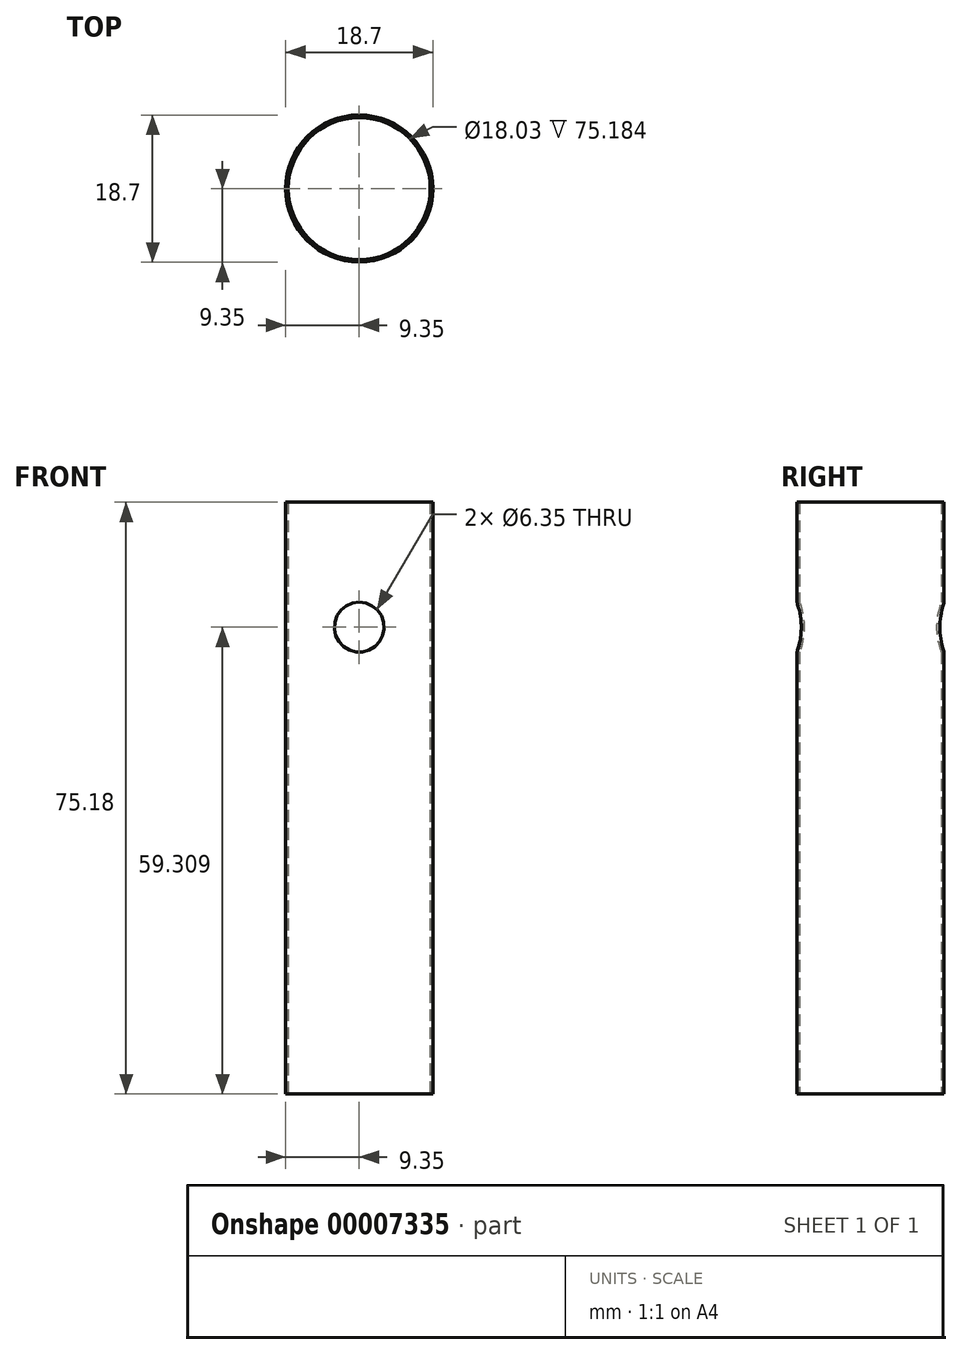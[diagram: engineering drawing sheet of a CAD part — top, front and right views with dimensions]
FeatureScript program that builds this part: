
annotation { "Feature Type Name" : "Feature", "Feature Type Description" : "" }
export const myFeature = defineFeature(function(context is Context, id is Id, definition is map)
    precondition{}
    {
        {
            var Q0;
            Q0=qCreatedBy(makeId("Front.planeOp"),FACE);
            var sketch = newSketch(context, id + "F0", { "sketchPlane" : qUnion([Q0])});
            skLineSegment(sketch, "E0.bottom", {"start": v(9.02, 0) * mm, "end": v(9.35, 0) * mm});
            skLineSegment(sketch, "E0.top", {"start": v(9.02, 75.18) * mm, "end": v(9.35, 75.18) * mm});
            skLineSegment(sketch, "E0.left", {"start": v(9.02, 0) * mm, "end": v(9.02, 75.18) * mm});
            skLineSegment(sketch, "E0.right", {"start": v(9.35, 0) * mm, "end": v(9.35, 75.18) * mm});
            skLineSegment(sketch, "E1", {"start": v(9.02, 0) * mm, "end": v(0, 0) * mm});
            skLineSegment(sketch, "E2", {"start": v(0, 0) * mm, "end": v(0, 75.18) * mm});
            skSolve(sketch);
        }
        {
            var Q0;
            Q0 = qSketchRegion(id + "F0", true);
            var Q1;
            Q1=sQuery(id+"F0.wireOp",EDGE,"E2");
            revolve(context, id + "F1", {"entities" : qUnion([Q0]), "axis" : qUnion([Q1]), "revolveType" : RevolveType.FULL});
        }
        {
            var Q0;
            Q0=qCreatedBy(makeId("Front.planeOp"),FACE);
            var sketch = newSketch(context, id + "F2", { "sketchPlane" : qUnion([Q0])});
            skLineSegment(sketch, "E3", {"start": v(0, 0) * mm, "end": v(0, 75.18) * mm});
            skCircle(sketch, "E4", {"center": v(0, 59.3) * mm, "radius": 3.18 * mm});
            skSolve(sketch);
        }
        {
            var Q0;
            Q0 = qSketchRegion(id + "F2", true);
            extrude(context, id + "F3", {"entities" : qUnion([Q0]), "operationType" : NewBodyOperationType.REMOVE, "endBound" : BoundingType.THROUGH_ALL, "oppositeDirection" : true, "depth" : 25.4 * mm});
        }
        {
            var Q0;
            Q0 = qSketchRegion(id + "F2", true);
            extrude(context, id + "F4", {"entities" : qUnion([Q0]), "operationType" : NewBodyOperationType.REMOVE, "endBound" : BoundingType.THROUGH_ALL, "depth" : 25.4 * mm});
        }
        {
            var Q0;
            Q0=qCreatedBy(makeId("Top.planeOp"),FACE);
            var sketch = newSketch(context, id + "F5", { "sketchPlane" : qUnion([Q0])});
            skCircle(sketch, "E5.0", {"center": v(0, 0) * mm, "radius": 9.35 * mm});
            skCircle(sketch, "E6", {"center": v(0, 0) * mm, "radius": 63.5 * mm});
            skLineSegment(sketch, "E7", {"start": v(0, 0) * mm, "end": v(0, 63.5) * mm});
            skLineSegment(sketch, "E8", {"start": v(0, 0) * mm, "end": v(-63.5, 0) * mm});
            skLineSegment(sketch, "E9", {"start": v(0, 0) * mm, "end": v(63.5, 0) * mm});
            skLineSegment(sketch, "E10", {"start": v(0, 0) * mm, "end": v(0, -63.5) * mm});
            skLineSegment(sketch, "E11", {"start": v(0, 0) * mm, "end": v(55, -31.75) * mm});
            skLineSegment(sketch, "E12.0.MirrorCS", {"start": v(0, 0) * mm, "end": v(-55, -31.75) * mm});
            skLineSegment(sketch, "E13", {"start": v(0, 0) * mm, "end": v(60.4, 19.62) * mm});
            skLineSegment(sketch, "E14", {"start": v(0, 0) * mm, "end": v(37.32, -51.37) * mm});
            skLineSegment(sketch, "E15.0.MirrorCS", {"start": v(0, 0) * mm, "end": v(-60.4, 19.62) * mm});
            skLineSegment(sketch, "E16.0.MirrorCS", {"start": v(0, 0) * mm, "end": v(-37.32, -51.37) * mm});
            skLineSegment(sketch, "E17", {"start": v(0, 0) * mm, "end": v(0.57, 0) * mm});
            skLineSegment(sketch, "E18", {"start": v(0.57, 0) * mm, "end": v(0.57, 63.5) * mm});
            skLineSegment(sketch, "E19.0.MirrorCS", {"start": v(-0.57, 0) * mm, "end": v(-0.57, 63.5) * mm});
            skLineSegment(sketch, "E20.0.MirrorCS", {"start": v(0, 0) * mm, "end": v(-0.57, 0) * mm});
            skCircle(sketch, "E21", {"center": v(2.74, 11.19) * mm, "radius": 2.17 * mm});
            skLineSegment(sketch, "E22", {"start": v(0, 0) * mm, "end": v(44.9, 44.9) * mm});
            skPoint(sketch, "E23", {"position": v(0, 9.35) * mm});
            skPoint(sketch, "E24", {"position": v(6.6, 6.6) * mm});
            skPoint(sketch, "E25", {"position": v(8.89, 2.89) * mm});
            skPoint(sketch, "E26", {"position": v(9.35, 0) * mm});
            skPoint(sketch, "E27", {"position": v(8.1, -4.67) * mm});
            skPoint(sketch, "E28", {"position": v(5.5, -7.56) * mm});
            skPoint(sketch, "E29", {"position": v(-8.89, 2.89) * mm});
            skPoint(sketch, "E30", {"position": v(-9.35, 0) * mm});
            skPoint(sketch, "E31", {"position": v(-8.1, -4.67) * mm});
            skPoint(sketch, "E32", {"position": v(-5.5, -7.56) * mm});
            skPoint(sketch, "E33", {"position": v(0, -9.35) * mm});
            skSolve(sketch);
        }
        {
            var Q0;
            Q0=sQuery(id+"F0.wireOp",VERTEX,"E2.end");
            var Q1;
            Q1=qCreatedBy(makeId("Origin.pointOp"),VERTEX);
            var Q2;
            Q2=sQuery(id+"F5.wireOp",VERTEX,"E21.center");
            cPlane(context, id + "F6", {"entities" : qUnion([Q0, Q1, Q2]), "cplaneType" : CPlaneType.THREE_POINT, "offset" : 152.4 * mm, "width" : 152.4 * mm, "height" : 152.4 * mm});
        }
    });
